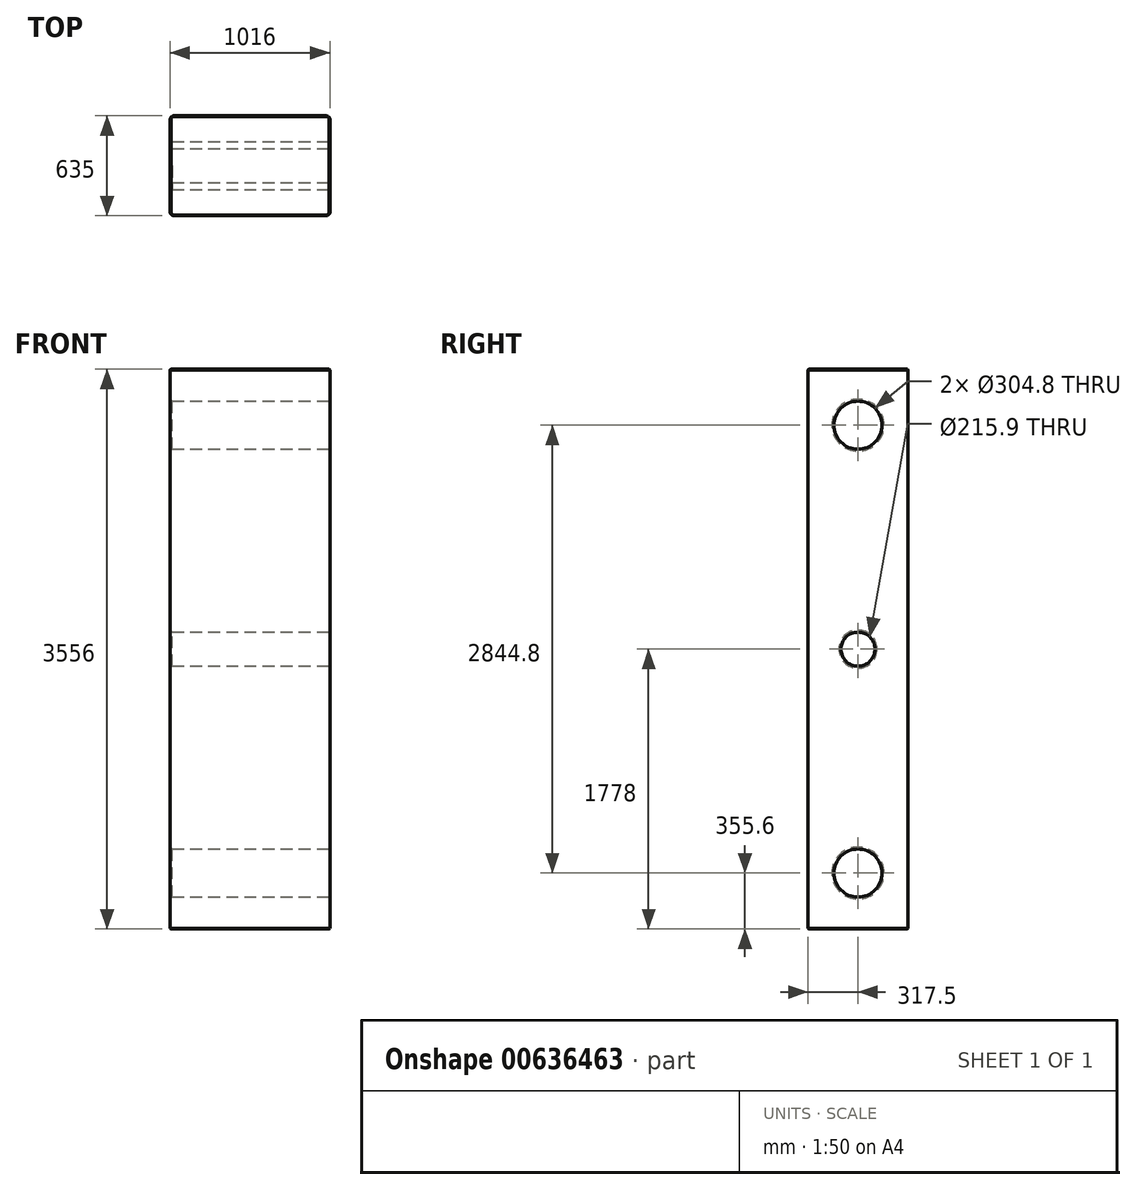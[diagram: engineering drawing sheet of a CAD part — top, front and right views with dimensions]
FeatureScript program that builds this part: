
annotation { "Feature Type Name" : "Feature", "Feature Type Description" : "" }
export const myFeature = defineFeature(function(context is Context, id is Id, definition is map)
    precondition{}
    {
        {
            var Q0;
            Q0=qCreatedBy(makeId("Top.planeOp"),FACE);
            var sketch = newSketch(context, id + "F0", { "sketchPlane" : qUnion([Q0])});
            skLineSegment(sketch, "E0.bottom", {"start": v(25.4, 0) * mm, "end": v(990.6, 0) * mm});
            skLineSegment(sketch, "E0.top", {"start": v(25.4, 635) * mm, "end": v(990.6, 635) * mm});
            skLineSegment(sketch, "E0.left", {"start": v(0, 25.4) * mm, "end": v(0, 609.6) * mm});
            skLineSegment(sketch, "E0.right", {"start": v(1016, 25.4) * mm, "end": v(1016, 609.6) * mm});
            skPoint(sketch, "E1.visualSharp", {"position": v(1016, 635) * mm});
            skArc(sketch, "E1.filletArc", {"start": v(1016, 609.6) * mm, "mid": v(1008.56, 627.56) * mm, "end": v(990.6, 635) * mm});
            skPoint(sketch, "E2.visualSharp", {"position": v(1016, 0) * mm});
            skArc(sketch, "E2.filletArc", {"start": v(990.6, 0) * mm, "mid": v(1008.56, 7.44) * mm, "end": v(1016, 25.4) * mm});
            skPoint(sketch, "E3.visualSharp", {"position": v(0, 0) * mm});
            skArc(sketch, "E3.filletArc", {"start": v(0, 25.4) * mm, "mid": v(7.44, 7.44) * mm, "end": v(25.4, 0) * mm});
            skPoint(sketch, "E4.visualSharp", {"position": v(0, 635) * mm});
            skArc(sketch, "E4.filletArc", {"start": v(25.4, 635) * mm, "mid": v(7.44, 627.56) * mm, "end": v(0, 609.6) * mm});
            skSolve(sketch);
        }
        {
            var Q0;
            Q0 = qSketchRegion(id + "F0", true);
            extrude(context, id + "F1", {"entities" : qUnion([Q0]), "depth" : 3556 * mm, "offsetDistance" : 25.4 * mm});
        }
        {
            var Q0;
            Q0=makeQuery(id+"F1.opExtrude","SWEPT_FACE",FACE,{"disambiguationData":[OSD([sQuery(id+"F0.wireOp",EDGE,"E0.right")])]});
            var sketch = newSketch(context, id + "F2", { "sketchPlane" : qUnion([Q0])});
            skLineSegment(sketch, "E5", {"start": v(317.5, 3556) * mm, "end": v(317.5, 0) * mm, "construction": true});
            skLineSegment(sketch, "E6", {"start": v(776.22, 1778) * mm, "end": v(-172.85, 1778) * mm, "construction": true});
            skPoint(sketch, "E6.startSnap0", {"position": v(609.6, 1778) * mm});
            skPoint(sketch, "E6.endSnap0", {"position": v(317.5, 1778) * mm});
            skCircle(sketch, "E7", {"center": v(317.5, 1778) * mm, "radius": 107.95 * mm});
            skCircle(sketch, "E8", {"center": v(317.5, 3200.4) * mm, "radius": 152.4 * mm});
            skCircle(sketch, "E9", {"center": v(317.5, 355.6) * mm, "radius": 152.4 * mm});
            skSolve(sketch);
        }
        {
            var Q0;
            Q0 = qSketchRegion(id + "F2", true);
            extrude(context, id + "F3", {"entities" : qUnion([Q0]), "operationType" : NewBodyOperationType.REMOVE, "endBound" : BoundingType.THROUGH_ALL, "oppositeDirection" : true, "depth" : 25.4 * mm, "offsetDistance" : 25.4 * mm});
        }
        {
            var Q0;
            Q0=makeQuery(id+"F3.boolean.opBoolean","COPY",EDGE,{"derivedFrom":makeQuery(id+"F3.opExtrude","CAP_EDGE",EDGE,{"disambiguationData":[OSD([sQuery(id+"F2.wireOp",EDGE,"E8")])],"isStart":true})});
            var Q1;
            Q1=makeQuery(id+"F3.boolean.opBoolean","COPY",EDGE,{"derivedFrom":makeQuery(id+"F3.opExtrude","CAP_EDGE",EDGE,{"disambiguationData":[OSD([sQuery(id+"F2.wireOp",EDGE,"E7")])],"isStart":true})});
            var Q2;
            Q2=makeQuery(id+"F3.boolean.opBoolean","COPY",EDGE,{"derivedFrom":makeQuery(id+"F3.opExtrude","CAP_EDGE",EDGE,{"disambiguationData":[OSD([sQuery(id+"F2.wireOp",EDGE,"E9")])],"isStart":true})});
            var Q3;
            Q3=makeQuery(id+"F3.boolean.opBoolean","INTERSECT",EDGE,{"derivedFrom":[makeQuery(id+"F1.opExtrude","SWEPT_FACE",FACE,{"disambiguationData":[OSD([sQuery(id+"F0.wireOp",EDGE,"E0.left")])]}),makeQuery(id+"F3.opExtrude","SWEPT_FACE",FACE,{"disambiguationData":[OSD([sQuery(id+"F2.wireOp",EDGE,"E8")])]})]});
            var Q4;
            Q4=makeQuery(id+"F3.boolean.opBoolean","INTERSECT",EDGE,{"derivedFrom":[makeQuery(id+"F1.opExtrude","SWEPT_FACE",FACE,{"disambiguationData":[OSD([sQuery(id+"F0.wireOp",EDGE,"E0.left")])]}),makeQuery(id+"F3.opExtrude","SWEPT_FACE",FACE,{"disambiguationData":[OSD([sQuery(id+"F2.wireOp",EDGE,"E7")])]})]});
            var Q5;
            Q5=makeQuery(id+"F3.boolean.opBoolean","INTERSECT",EDGE,{"derivedFrom":[makeQuery(id+"F1.opExtrude","SWEPT_FACE",FACE,{"disambiguationData":[OSD([sQuery(id+"F0.wireOp",EDGE,"E0.left")])]}),makeQuery(id+"F3.opExtrude","SWEPT_FACE",FACE,{"disambiguationData":[OSD([sQuery(id+"F2.wireOp",EDGE,"E9")])]})]});
            chamfer(context, id + "F4", {"entities" : qUnion([Q0, Q1, Q2, Q3, Q4, Q5]), "width" : 12.7 * mm, "tangentPropagation" : true});
        }
        {
            var Q0;
            Q0=makeQuery(id+"F1.opExtrude","CAP_EDGE",EDGE,{"disambiguationData":[OSD([sQuery(id+"F0.wireOp",EDGE,"E0.bottom")])],"isStart":false});
            var Q1;
            Q1=makeQuery(id+"F1.opExtrude","CAP_EDGE",EDGE,{"disambiguationData":[OSD([sQuery(id+"F0.wireOp",EDGE,"E0.left")])],"isStart":false});
            var Q2;
            Q2=makeQuery(id+"F1.opExtrude","CAP_EDGE",EDGE,{"disambiguationData":[OSD([sQuery(id+"F0.wireOp",EDGE,"E0.top")])],"isStart":false});
            var Q3;
            Q3=makeQuery(id+"F1.opExtrude","CAP_EDGE",EDGE,{"disambiguationData":[OSD([sQuery(id+"F0.wireOp",EDGE,"E0.right")])],"isStart":false});
            chamfer(context, id + "F5", {"entities" : qUnion([Q0, Q1, Q2, Q3]), "width" : 5.08 * mm, "tangentPropagation" : true});
        }
        {
            var Q0;
            Q0=makeQuery(id+"F1.opExtrude","CAP_EDGE",EDGE,{"disambiguationData":[OSD([sQuery(id+"F0.wireOp",EDGE,"E0.top")])],"isStart":true});
            var Q1;
            Q1=makeQuery(id+"F1.opExtrude","CAP_EDGE",EDGE,{"disambiguationData":[OSD([sQuery(id+"F0.wireOp",EDGE,"E0.right")])],"isStart":true});
            var Q2;
            Q2=makeQuery(id+"F1.opExtrude","CAP_EDGE",EDGE,{"disambiguationData":[OSD([sQuery(id+"F0.wireOp",EDGE,"E0.bottom")])],"isStart":true});
            var Q3;
            Q3=makeQuery(id+"F1.opExtrude","CAP_EDGE",EDGE,{"disambiguationData":[OSD([sQuery(id+"F0.wireOp",EDGE,"E0.left")])],"isStart":true});
            chamfer(context, id + "F6", {"entities" : qUnion([Q0, Q1, Q2, Q3]), "width" : 5.08 * mm, "tangentPropagation" : true});
        }
    });
